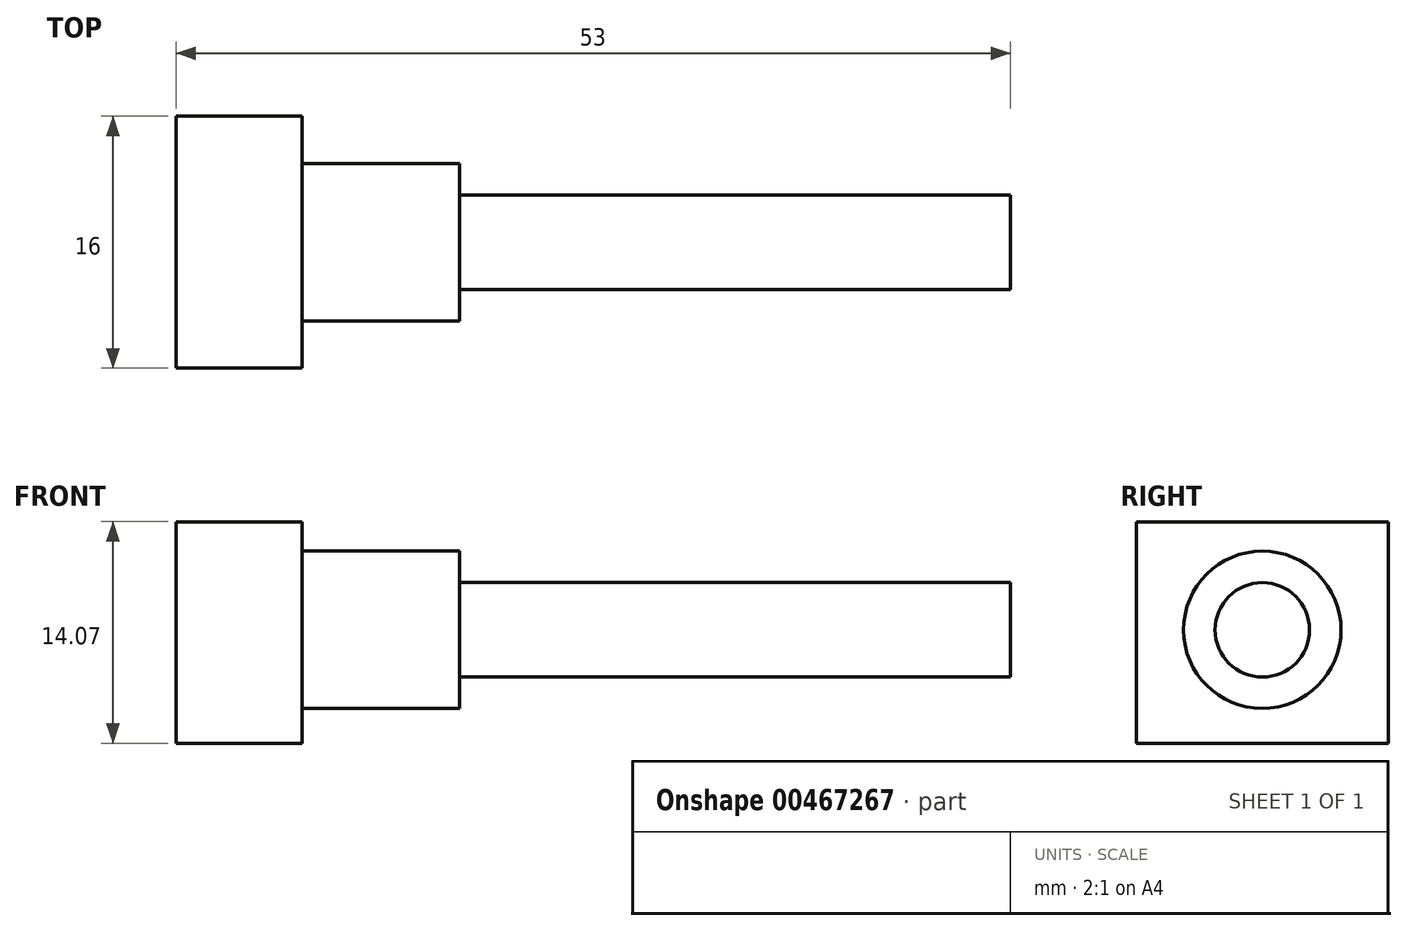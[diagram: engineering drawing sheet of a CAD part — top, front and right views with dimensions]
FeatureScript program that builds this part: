
annotation { "Feature Type Name" : "Feature", "Feature Type Description" : "" }
export const myFeature = defineFeature(function(context is Context, id is Id, definition is map)
    precondition{}
    {
        {
            var Q0;
            Q0=qCreatedBy(makeId("Right.planeOp"),FACE);
            var sketch = newSketch(context, id + "F0", { "sketchPlane" : qUnion([Q0])});
            skCircle(sketch, "E0", {"center": v(0, 0) * mm, "radius": 5 * mm});
            skSolve(sketch);
        }
        {
            var Q0;
            Q0=qSketchRegion(id+"F0",true);
            extrude(context, id + "F1", {"entities" : qUnion([Q0]), "depth" : 10 * mm});
        }
        {
            var Q0;
            Q0=makeQuery(id+"F1.opExtrude","CAP_FACE",FACE,{"disambiguationData":[OSD([sQuery(id+"F0.wireOp",EDGE,"E0")])],"isStart":false});
            var sketch = newSketch(context, id + "F2", { "sketchPlane" : qUnion([Q0])});
            skCircle(sketch, "E1", {"center": v(0, 0) * mm, "radius": 3 * mm});
            skSolve(sketch);
        }
        {
            var Q0;
            Q0=qSketchRegion(id+"F2",true);
            extrude(context, id + "F3", {"entities" : qUnion([Q0]), "operationType" : NewBodyOperationType.ADD, "depth" : 35 * mm});
        }
        {
            var Q0;
            Q0=makeQuery(id+"F1.opExtrude","CAP_FACE",FACE,{"disambiguationData":[OSD([sQuery(id+"F0.wireOp",EDGE,"E0")])],"isStart":true});
            var sketch = newSketch(context, id + "F4", { "sketchPlane" : qUnion([Q0])});
            skLineSegment(sketch, "E2.bottom", {"start": v(-8, 6.87) * mm, "end": v(8, 6.87) * mm});
            skLineSegment(sketch, "E2.top", {"start": v(-8, -7.2) * mm, "end": v(8, -7.2) * mm});
            skLineSegment(sketch, "E2.left", {"start": v(-8, 6.87) * mm, "end": v(-8, -7.2) * mm});
            skLineSegment(sketch, "E2.right", {"start": v(8, 6.87) * mm, "end": v(8, -7.2) * mm});
            skSolve(sketch);
        }
        {
            var Q0;
            Q0=qSketchRegion(id+"F4",true);
            extrude(context, id + "F5", {"entities" : qUnion([Q0]), "operationType" : NewBodyOperationType.ADD, "depth" : 8 * mm});
        }
    });
